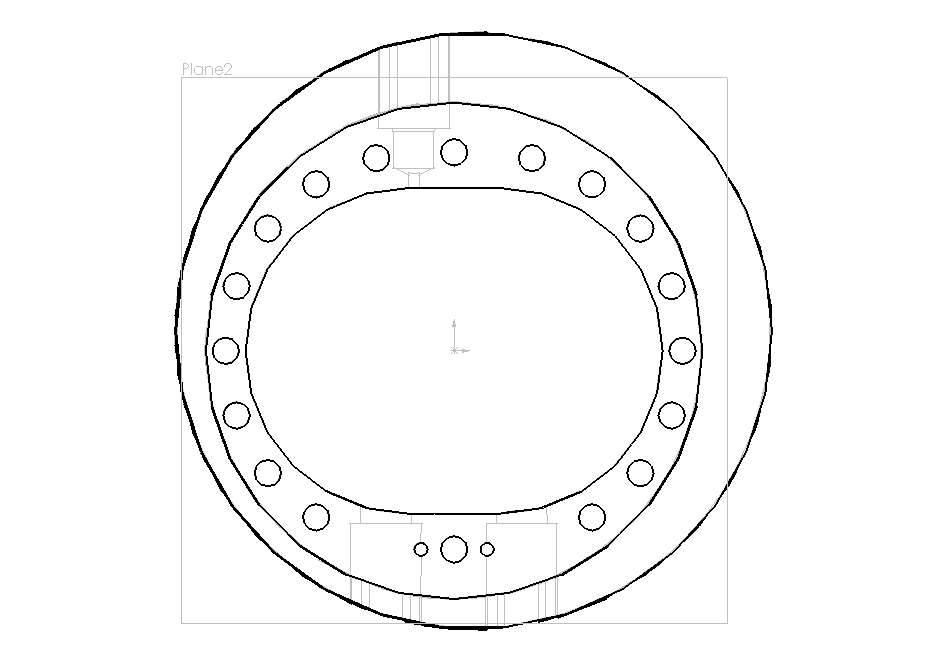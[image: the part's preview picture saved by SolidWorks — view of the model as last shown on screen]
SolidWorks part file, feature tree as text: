
SOLIDWORKS PART (.sldprt)
format: sldprt  version: not decoded by parser v0  size: 800,768 bytes
history: native  units: mm
features: sketch x7, cut_extrude x6, plane x2, material x1, cut_revolve x1 + 6 further entries (+12 scaffold rows collapsed)
feature tree (35):
  scaffold x12  (default folders/planes/origin — collapsed)
  material  "Material <not specified>"
  "1.zylinder_fin<3>@1.zylinder_combined-"
  "1.zylinder_fin<1>@1.zylinder_combined-"
  "1.zylinder_fin<2>@1.zylinder_combined-"
  "1.zylinder_fin<5>@1.zylinder_combined-"
  "1.zylinder_fin<6>@1.zylinder_combined-"
  "1.zylinder_base<1>@1.zylinder_combined-"
  sketch  "Sketch2"  dims[c1.D2=49.2mm c1.D4=49.2mm c1.D17=4.0mm c1.D13=4.0mm c1.D1=6.9mm c1.D3=6.9mm c1.D5=13.8mm c1.D6=13.8mm c2.D5=6.9mm c2.D6=6.9mm c2.D7=31.0mm c2.D8=31.0mm c2.D9=30.0mm c2.D10=30.0mm c2.D11=4.5mm c3.D10=30.0mm c3.D9=4.5mm c3.D12=30.0mm c3.D13=~27.010985mm c4.D13=~162.410467deg c5.D13=~29.092008mm c6.D13=~166.293086deg c7.D13=30.0mm c8.D13=~159.137743deg c9.D13=~35.555547mm c10.D13=19.0deg c10.D14=~42.317455mm c11.D14=~146.816918deg c12.D14=~42.317455mm c13.D14=19.0deg c13.D15=~125.826232deg c14.D15=~38.234035mm c15.D15=19.0deg c15.D16=~38.234035mm c16.D16=19.0deg c16.D13=19.0deg c16.D14=19.0deg c16.D15=19.0deg]
  sketch  "Sketch3"
  cut_extrude  "Cut-Extrude2"  Depth=18mm
  plane  "Plane1"  Offset=1.5mm
  sketch  "Sketch5"  dims[D4=8.0mm D5=8.0mm D6=11.0mm D7=11.0mm D1=9.0mm D2=10.25mm D3=10.25mm]
  sketch  "Sketch9"  dims[c1.D1=6.0mm c1.D2=9.0mm c1.D3=1.6mm c1.D4=3.6mm c1.D5=0.7mm c2.D3=0.8mm c2.D4=0.9mm c2.D5=3.6mm c3.D4=0.8mm c3.D5=1.8mm c3.D6=1.8mm c3.D1=6.0mm c3.D2=9.0mm c3.D3=0.8mm c4.D4=0.8mm c4.D5=1.6mm c4.D6=1.6mm]
  plane  "Plane2"
  sketch  "Sketch11"  dims[c1.D1=6.0mm c1.D2=5.5mm c1.D3=5.5mm c2.D2=11.0mm c2.D3=6.35mm c3.D2=11.0mm c3.D3=6.35mm c3.D1=6.0mm c3.D4=4.0mm c3.D5=6.0mm c3.D6=1.6mm c3.D7=5.5mm c3.D8=7.0mm c3.D9=1.25mm c4.D2=5.5mm c4.D3=3.175mm c4.D6=0.8mm c4.D8=7.25mm c4.D9=3.5mm]
  cut_revolve  "Cut-Revolve1"  Angle=360deg
  cut_extrude  "Cut-Extrude5"  [1 undecoded]
  cut_extrude  "Cut-Extrude6"  [1 undecoded]
  sketch  "Sketch12"  dims[c1.D3=4.0mm c1.D4=4.0mm c1.D9=2.0mm c1.D10=2.0mm c1.D11=4.0mm c1.D1=30.0mm c1.D2=30.0mm c1.D5=5.0mm c1.D6=5.0mm c1.D7=30.0mm c1.D8=30.0mm c2.D10=~11.265744mm c2.D11=~60.827625mm]
  cut_extrude  "Cut-Extrude8"  Depth=20mm
  cut_extrude  "Cut-Extrude9"  [1 undecoded]
  sketch  "Sketch5<3>"  dims[D1=20.0mm]
  cut_extrude  "Cut-Extrude10"  Depth=20mm
decode coverage: 10 of 14 modeling features carry decoded parameters; 6 rows unclassified (native names shown)
note: ~ marks probable driven/reference dimensions
note: 3 parameter values undecoded
summary: no parameter record found for 3 features
note: suppression state not decoded; provenance and decode notes live in map.json
